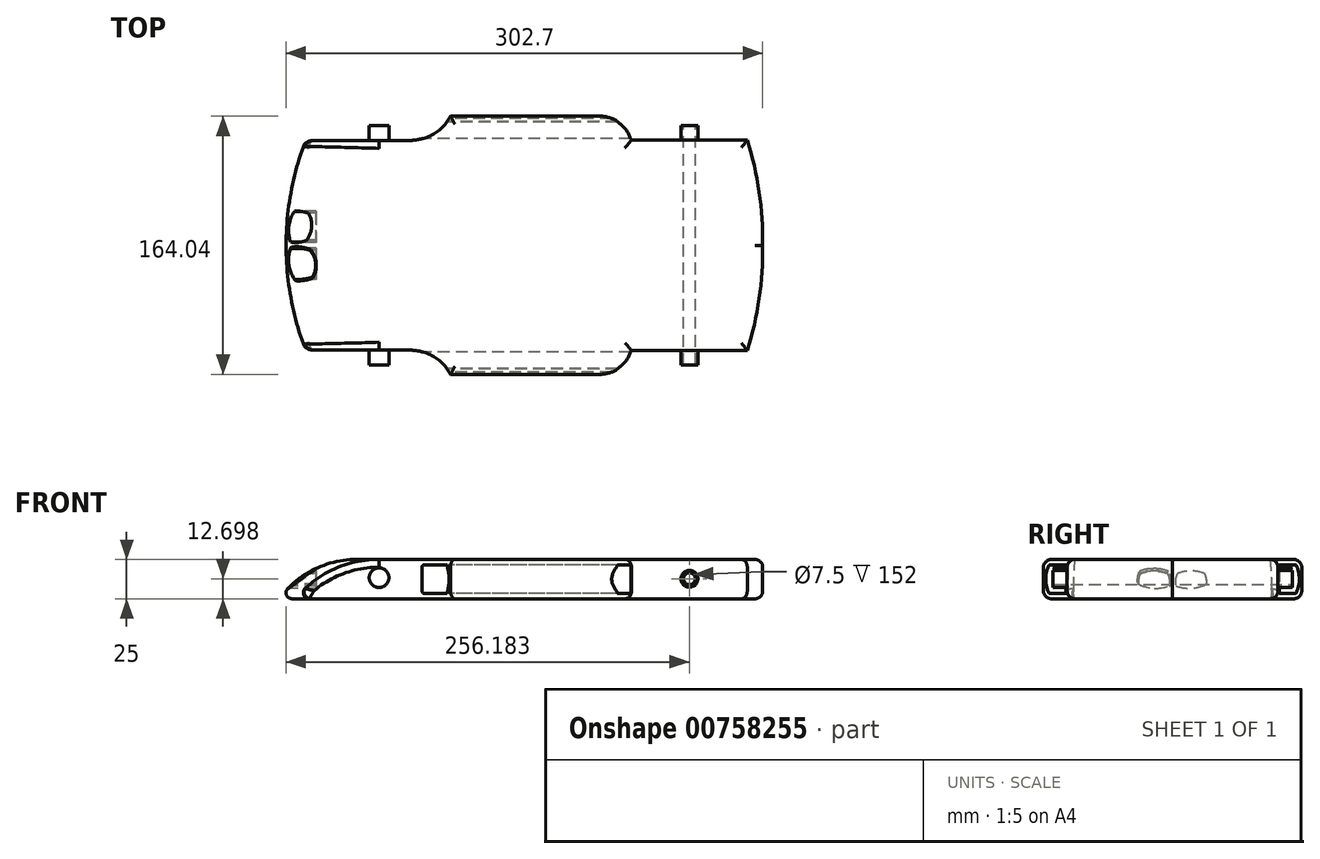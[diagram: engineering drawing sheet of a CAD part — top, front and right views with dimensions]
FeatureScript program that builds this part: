
annotation { "Feature Type Name" : "Feature", "Feature Type Description" : "" }
export const myFeature = defineFeature(function(context is Context, id is Id, definition is map)
    precondition{}
    {
        {
            var Q0;
            Q0=qCreatedBy(makeId("Top.planeOp"),FACE);
            var sketch = newSketch(context, id + "F0", { "sketchPlane" : qUnion([Q0])});
            skArc(sketch, "E0", {"start": v(-145.93, 0) * mm, "mid": v(-142.88, -33.83) * mm, "end": v(-133.85, -66.57) * mm});
            skLineSegment(sketch, "E1", {"start": v(-133.85, -66.57) * mm, "end": v(-63.46, -66.57) * mm});
            skArc(sketch, "E2", {"start": v(-37.18, -82.02) * mm, "mid": v(-48.22, -70.72) * mm, "end": v(-63.46, -66.57) * mm});
            skLineSegment(sketch, "E3", {"start": v(-37.18, -82.02) * mm, "end": v(57.44, -82.02) * mm});
            skArc(sketch, "E4", {"start": v(57.44, -82.02) * mm, "mid": v(70.1, -77.84) * mm, "end": v(77.8, -66.96) * mm});
            skLineSegment(sketch, "E5", {"start": v(77.8, -66.96) * mm, "end": v(151.34, -66.96) * mm});
            skArc(sketch, "E6", {"start": v(151.34, -66.96) * mm, "mid": v(158.9, -33.87) * mm, "end": v(161.11, 0) * mm});
            skArc(sketch, "E7.MirrorCS", {"start": v(-145.93, 0) * mm, "mid": v(-142.88, 33.83) * mm, "end": v(-133.85, 66.57) * mm});
            skLineSegment(sketch, "E8.MirrorCS", {"start": v(-133.85, 66.57) * mm, "end": v(-63.46, 66.57) * mm});
            skArc(sketch, "E9.MirrorCS", {"start": v(-37.18, 82.02) * mm, "mid": v(-48.22, 70.72) * mm, "end": v(-63.46, 66.57) * mm});
            skLineSegment(sketch, "E10.MirrorCS", {"start": v(-37.18, 82.02) * mm, "end": v(57.44, 82.02) * mm});
            skArc(sketch, "E11.MirrorCS", {"start": v(57.44, 82.02) * mm, "mid": v(70.1, 77.84) * mm, "end": v(77.8, 66.96) * mm});
            skLineSegment(sketch, "E12.MirrorCS", {"start": v(77.8, 66.96) * mm, "end": v(151.34, 66.96) * mm});
            skArc(sketch, "E13.MirrorCS", {"start": v(151.34, 66.96) * mm, "mid": v(158.9, 33.87) * mm, "end": v(161.11, 0) * mm});
            skSolve(sketch);
        }
        {
            var Q0;
            Q0 = qSketchRegion(id + "F0", true);
            extrude(context, id + "F1", {"entities" : qUnion([Q0]), "depth" : 25 * mm, "offsetDistance" : 25 * mm});
        }
        {
            var Q0;
            Q0=makeQuery(id+"F1.opExtrude","CAP_EDGE",EDGE,{"disambiguationData":[OSD([sQuery(id+"F0.wireOp",EDGE,"E0")])],"isStart":false});
            fillet(context, id + "F2", {"entities" : qUnion([Q0]), "radius" : 61.08 * mm, "tangentPropagation" : true, "allowEdgeOverflow" : false});
        }
        {
            var Q0;
            {var subQ0=sQuery(id+"F0.wireOp",EDGE,"E0");Q0=makeQuery(id+"F2.opFillet","BLEND_EDGE",EDGE,{"blendedFrom":[makeQuery(id+"F1.opExtrude","CAP_EDGE",EDGE,{"disambiguationData":[OSD([subQ0])],"isStart":false}),makeQuery(id+"F1.opExtrude","CAP_FACE",FACE,{"disambiguationData":[OSD([subQ0,sQuery(id+"F0.wireOp",EDGE,"E1"),sQuery(id+"F0.wireOp",EDGE,"E2"),sQuery(id+"F0.wireOp",EDGE,"E3"),sQuery(id+"F0.wireOp",EDGE,"E4"),sQuery(id+"F0.wireOp",EDGE,"E5"),sQuery(id+"F0.wireOp",EDGE,"E6"),sQuery(id+"F0.wireOp",EDGE,"E7.MirrorCS"),sQuery(id+"F0.wireOp",EDGE,"E8.MirrorCS"),sQuery(id+"F0.wireOp",EDGE,"E9.MirrorCS"),sQuery(id+"F0.wireOp",EDGE,"E10.MirrorCS"),sQuery(id+"F0.wireOp",EDGE,"E11.MirrorCS"),sQuery(id+"F0.wireOp",EDGE,"E12.MirrorCS"),sQuery(id+"F0.wireOp",EDGE,"E13.MirrorCS")])],"isStart":true})],"blendedInto":[makeQuery(id+"F1.opExtrude","CAP_FACE",FACE,{"disambiguationData":[OSD([subQ0,sQuery(id+"F0.wireOp",EDGE,"E1"),sQuery(id+"F0.wireOp",EDGE,"E2"),sQuery(id+"F0.wireOp",EDGE,"E3"),sQuery(id+"F0.wireOp",EDGE,"E4"),sQuery(id+"F0.wireOp",EDGE,"E5"),sQuery(id+"F0.wireOp",EDGE,"E6"),sQuery(id+"F0.wireOp",EDGE,"E7.MirrorCS"),sQuery(id+"F0.wireOp",EDGE,"E8.MirrorCS"),sQuery(id+"F0.wireOp",EDGE,"E9.MirrorCS"),sQuery(id+"F0.wireOp",EDGE,"E10.MirrorCS"),sQuery(id+"F0.wireOp",EDGE,"E11.MirrorCS"),sQuery(id+"F0.wireOp",EDGE,"E12.MirrorCS"),sQuery(id+"F0.wireOp",EDGE,"E13.MirrorCS")])],"isStart":true})]});}
            fillet(context, id + "F3", {"entities" : qUnion([Q0]), "radius" : 3.8 * mm, "tangentPropagation" : true, "allowEdgeOverflow" : false});
        }
        {
            var Q0;
            Q0=makeQuery(id+"F1.opExtrude","CAP_EDGE",EDGE,{"disambiguationData":[OSD([sQuery(id+"F0.wireOp",EDGE,"E10.MirrorCS")])],"isStart":false});
            var Q1;
            Q1=makeQuery(id+"F1.opExtrude","CAP_EDGE",EDGE,{"disambiguationData":[OSD([sQuery(id+"F0.wireOp",EDGE,"E10.MirrorCS")])],"isStart":true});
            var Q2;
            Q2=makeQuery(id+"F1.opExtrude","CAP_EDGE",EDGE,{"disambiguationData":[OSD([sQuery(id+"F0.wireOp",EDGE,"E9.MirrorCS")])],"isStart":false});
            var Q3;
            Q3=makeQuery(id+"F1.opExtrude","CAP_EDGE",EDGE,{"disambiguationData":[OSD([sQuery(id+"F0.wireOp",EDGE,"E3")])],"isStart":false});
            var Q4;
            Q4=makeQuery(id+"F1.opExtrude","CAP_EDGE",EDGE,{"disambiguationData":[OSD([sQuery(id+"F0.wireOp",EDGE,"E3")])],"isStart":true});
            var Q5;
            Q5=makeQuery(id+"F1.opExtrude","CAP_EDGE",EDGE,{"disambiguationData":[OSD([sQuery(id+"F0.wireOp",EDGE,"E2")])],"isStart":true});
            var Q6;
            Q6=makeQuery(id+"F1.opExtrude","CAP_EDGE",EDGE,{"disambiguationData":[OSD([sQuery(id+"F0.wireOp",EDGE,"E5")])],"isStart":true});
            var Q7;
            Q7=makeQuery(id+"F1.opExtrude","CAP_EDGE",EDGE,{"disambiguationData":[OSD([sQuery(id+"F0.wireOp",EDGE,"E5")])],"isStart":false});
            var Q8;
            Q8=makeQuery(id+"F1.opExtrude","CAP_EDGE",EDGE,{"disambiguationData":[OSD([sQuery(id+"F0.wireOp",EDGE,"E12.MirrorCS")])],"isStart":true});
            var Q9;
            Q9=makeQuery(id+"F1.opExtrude","CAP_EDGE",EDGE,{"disambiguationData":[OSD([sQuery(id+"F0.wireOp",EDGE,"E12.MirrorCS")])],"isStart":false});
            var Q10;
            Q10=makeQuery(id+"F1.opExtrude","CAP_EDGE",EDGE,{"disambiguationData":[OSD([sQuery(id+"F0.wireOp",EDGE,"E6")])],"isStart":false});
            var Q11;
            Q11=makeQuery(id+"F1.opExtrude","CAP_EDGE",EDGE,{"disambiguationData":[OSD([sQuery(id+"F0.wireOp",EDGE,"E6")])],"isStart":true});
            fillet(context, id + "F4", {"entities" : qUnion([Q0, Q1, Q2, Q3, Q4, Q5, Q6, Q7, Q8, Q9, Q10, Q11]), "radius" : 5 * mm, "tangentPropagation" : true, "allowEdgeOverflow" : false});
        }
        {
            var Q0;
            Q0=qCreatedBy(makeId("Front.planeOp"),FACE);
            var sketch = newSketch(context, id + "F5", { "sketchPlane" : qUnion([Q0])});
            skCircle(sketch, "E14", {"center": v(114.62, 12.7) * mm, "radius": 5.35 * mm});
            skCircle(sketch, "E15", {"center": v(114.62, 12.7) * mm, "radius": 3.75 * mm});
            skSolve(sketch);
        }
        {
            var Q0;
            Q0 = qSketchRegion(id + "F5", true);
            extrude(context, id + "F6", {"entities" : qUnion([Q0]), "operationType" : NewBodyOperationType.ADD, "depth" : 76 * mm, "offsetDistance" : 25 * mm, "hasSecondDirection" : true, "secondDirectionOppositeDirection" : true, "secondDirectionDepth" : 76 * mm});
        }
        {
            var Q0;
            Q0=makeQuery(id+"F6.boolean.opBoolean","SPLIT",FACE,{"disambiguationData":[TD([makeQuery(id+"F6.opExtrude","SWEPT_FACE",FACE,{"disambiguationData":[OSD([sQuery(id+"F5.wireOp",EDGE,"E15")])]})])],"derivedFrom":makeQuery(id+"F1.opExtrude","SWEPT_FACE",FACE,{"disambiguationData":[OSD([sQuery(id+"F0.wireOp",EDGE,"E5")])]})});
            extrude(context, id + "F7", {"entities" : qUnion([Q0]), "operationType" : NewBodyOperationType.REMOVE, "endBound" : BoundingType.THROUGH_ALL, "oppositeDirection" : true, "depth" : 25 * mm, "offsetDistance" : 25 * mm});
        }
        {
            var Q0;
            Q0=qCreatedBy(makeId("Right.planeOp"),FACE);
            cPlane(context, id + "F8", {"entities" : qUnion([Q0]), "cplaneType" : CPlaneType.OFFSET, "offset" : 137 * mm, "oppositeDirection" : true, "width" : 150 * mm, "height" : 150 * mm});
        }
        {
            var Q0;
            Q0=qCreatedBy(id+"F8.planeOp",FACE);
            var sketch = newSketch(context, id + "F9", { "sketchPlane" : qUnion([Q0])});
            skPoint(sketch, "E16.start.orphan", {"position": v(0, 8.15) * mm});
            skArc(sketch, "E17", {"start": v(-2.08, 8.15) * mm, "mid": v(-1.81, 12.22) * mm, "end": v(-3.18, 16.06) * mm});
            skArc(sketch, "E18", {"start": v(-3.18, 16.06) * mm, "mid": v(-11.77, 17.65) * mm, "end": v(-20.37, 16.06) * mm});
            skArc(sketch, "E19", {"start": v(-20.37, 16.06) * mm, "mid": v(-21.52, 12.78) * mm, "end": v(-21.59, 9.3) * mm});
            skArc(sketch, "E20", {"start": v(-21.59, 9.3) * mm, "mid": v(-11.96, 6.7) * mm, "end": v(-2.08, 8.15) * mm});
            skArc(sketch, "E21.MirrorCS", {"start": v(3.18, 16.06) * mm, "mid": v(11.77, 17.65) * mm, "end": v(20.37, 16.06) * mm});
            skArc(sketch, "E22.MirrorCS", {"start": v(20.37, 16.06) * mm, "mid": v(21.52, 12.78) * mm, "end": v(21.59, 9.3) * mm});
            skArc(sketch, "E23.MirrorCS", {"start": v(21.59, 9.3) * mm, "mid": v(11.96, 6.7) * mm, "end": v(2.08, 8.15) * mm});
            skArc(sketch, "E24.MirrorCS", {"start": v(2.08, 8.15) * mm, "mid": v(1.81, 12.22) * mm, "end": v(3.18, 16.06) * mm});
            skSolve(sketch);
        }
        {
            var Q0;
            Q0 = qSketchRegion(id + "F9", true);
            extrude(context, id + "F10", {"entities" : qUnion([Q0]), "operationType" : NewBodyOperationType.REMOVE, "depth" : 14.6 * mm, "offsetDistance" : 25 * mm, "hasSecondDirection" : true, "secondDirectionOppositeDirection" : true, "secondDirectionDepth" : 7 * mm});
        }
        {
            var Q0;
            Q0=makeQuery(id+"F10.boolean.opBoolean","INTERSECT",EDGE,{"derivedFrom":[makeQuery(id+"F2.opFillet","BLEND_FACE",FACE,{"disambiguationData":[OSD([sQuery(id+"F0.wireOp",EDGE,"E0")])]}),makeQuery(id+"F10.opExtrude","SWEPT_FACE",FACE,{"disambiguationData":[OSD([sQuery(id+"F9.wireOp",EDGE,"E22.MirrorCS")])]})]});
            var Q1;
            Q1=makeQuery(id+"F10.boolean.opBoolean","INTERSECT",EDGE,{"derivedFrom":[makeQuery(id+"F2.opFillet","BLEND_FACE",FACE,{"disambiguationData":[OSD([sQuery(id+"F0.wireOp",EDGE,"E0")])]}),makeQuery(id+"F10.opExtrude","SWEPT_FACE",FACE,{"disambiguationData":[OSD([sQuery(id+"F9.wireOp",EDGE,"E24.MirrorCS")])]})]});
            var Q2;
            Q2=makeQuery(id+"F10.boolean.opBoolean","INTERSECT",EDGE,{"derivedFrom":[makeQuery(id+"F2.opFillet","BLEND_FACE",FACE,{"disambiguationData":[OSD([sQuery(id+"F0.wireOp",EDGE,"E0")])]}),makeQuery(id+"F10.opExtrude","SWEPT_FACE",FACE,{"disambiguationData":[OSD([sQuery(id+"F9.wireOp",EDGE,"E21.MirrorCS")])]})]});
            var Q3;
            {var subQ0=sQuery(id+"F0.wireOp",EDGE,"E0");Q3=makeQuery(id+"F3.opFillet","BLEND_EDGE",EDGE,{"blendedFrom":[makeQuery(id+"F2.opFillet","BLEND_EDGE",EDGE,{"blendedFrom":[makeQuery(id+"F1.opExtrude","CAP_EDGE",EDGE,{"disambiguationData":[OSD([subQ0])],"isStart":false}),makeQuery(id+"F1.opExtrude","CAP_FACE",FACE,{"disambiguationData":[OSD([subQ0,sQuery(id+"F0.wireOp",EDGE,"E1"),sQuery(id+"F0.wireOp",EDGE,"E2"),sQuery(id+"F0.wireOp",EDGE,"E3"),sQuery(id+"F0.wireOp",EDGE,"E4"),sQuery(id+"F0.wireOp",EDGE,"E5"),sQuery(id+"F0.wireOp",EDGE,"E6"),sQuery(id+"F0.wireOp",EDGE,"E7.MirrorCS"),sQuery(id+"F0.wireOp",EDGE,"E8.MirrorCS"),sQuery(id+"F0.wireOp",EDGE,"E9.MirrorCS"),sQuery(id+"F0.wireOp",EDGE,"E10.MirrorCS"),sQuery(id+"F0.wireOp",EDGE,"E11.MirrorCS"),sQuery(id+"F0.wireOp",EDGE,"E12.MirrorCS"),sQuery(id+"F0.wireOp",EDGE,"E13.MirrorCS")])],"isStart":true})],"blendedInto":[makeQuery(id+"F1.opExtrude","CAP_FACE",FACE,{"disambiguationData":[OSD([subQ0,sQuery(id+"F0.wireOp",EDGE,"E1"),sQuery(id+"F0.wireOp",EDGE,"E2"),sQuery(id+"F0.wireOp",EDGE,"E3"),sQuery(id+"F0.wireOp",EDGE,"E4"),sQuery(id+"F0.wireOp",EDGE,"E5"),sQuery(id+"F0.wireOp",EDGE,"E6"),sQuery(id+"F0.wireOp",EDGE,"E7.MirrorCS"),sQuery(id+"F0.wireOp",EDGE,"E8.MirrorCS"),sQuery(id+"F0.wireOp",EDGE,"E9.MirrorCS"),sQuery(id+"F0.wireOp",EDGE,"E10.MirrorCS"),sQuery(id+"F0.wireOp",EDGE,"E11.MirrorCS"),sQuery(id+"F0.wireOp",EDGE,"E12.MirrorCS"),sQuery(id+"F0.wireOp",EDGE,"E13.MirrorCS")])],"isStart":true})]}),makeQuery(id+"F2.opFillet","BLEND_FACE",FACE,{"disambiguationData":[OSD([subQ0])]})],"blendedInto":[makeQuery(id+"F2.opFillet","BLEND_FACE",FACE,{"disambiguationData":[OSD([subQ0])]})]});}
            var Q4;
            Q4=makeQuery(id+"F10.boolean.opBoolean","INTERSECT",EDGE,{"derivedFrom":[makeQuery(id+"F2.opFillet","BLEND_FACE",FACE,{"disambiguationData":[OSD([sQuery(id+"F0.wireOp",EDGE,"E0")])]}),makeQuery(id+"F10.opExtrude","SWEPT_FACE",FACE,{"disambiguationData":[OSD([sQuery(id+"F9.wireOp",EDGE,"E18")])]})]});
            var Q5;
            Q5=makeQuery(id+"F10.boolean.opBoolean","INTERSECT",EDGE,{"derivedFrom":[makeQuery(id+"F2.opFillet","BLEND_FACE",FACE,{"disambiguationData":[OSD([sQuery(id+"F0.wireOp",EDGE,"E0")])]}),makeQuery(id+"F10.opExtrude","SWEPT_FACE",FACE,{"disambiguationData":[OSD([sQuery(id+"F9.wireOp",EDGE,"E19")])]})]});
            var Q6;
            Q6=makeQuery(id+"F10.boolean.opBoolean","INTERSECT",EDGE,{"derivedFrom":[makeQuery(id+"F2.opFillet","BLEND_FACE",FACE,{"disambiguationData":[OSD([sQuery(id+"F0.wireOp",EDGE,"E0")])]}),makeQuery(id+"F10.opExtrude","SWEPT_FACE",FACE,{"disambiguationData":[OSD([sQuery(id+"F9.wireOp",EDGE,"E17")])]})]});
            fillet(context, id + "F11", {"entities" : qUnion([Q0, Q1, Q2, Q3, Q4, Q5, Q6]), "radius" : 0.81 * mm, "tangentPropagation" : true, "allowEdgeOverflow" : false});
        }
        {
            var Q0;
            Q0=qCreatedBy(makeId("Right.planeOp"),FACE);
            var sketch = newSketch(context, id + "F12", { "sketchPlane" : qUnion([Q0])});
            skArc(sketch, "E25", {"start": v(-78.45, 21.45) * mm, "mid": v(-80.55, 12.4) * mm, "end": v(-78.38, 3.36) * mm});
            skLineSegment(sketch, "E26", {"start": v(-78.38, 3.36) * mm, "end": v(-67.7, 3.36) * mm});
            skLineSegment(sketch, "E27", {"start": v(-67.7, 3.36) * mm, "end": v(-67.7, 21.45) * mm});
            skLineSegment(sketch, "E28", {"start": v(-67.7, 21.45) * mm, "end": v(-78.45, 21.45) * mm});
            skLineSegment(sketch, "E29.MirrorCS", {"start": v(67.7, 21.45) * mm, "end": v(78.45, 21.45) * mm});
            skArc(sketch, "E30.MirrorCS", {"start": v(78.45, 21.45) * mm, "mid": v(80.55, 12.4) * mm, "end": v(78.38, 3.36) * mm});
            skLineSegment(sketch, "E31.MirrorCS", {"start": v(78.38, 3.36) * mm, "end": v(67.7, 3.36) * mm});
            skLineSegment(sketch, "E32.MirrorCS", {"start": v(67.7, 3.36) * mm, "end": v(67.7, 21.45) * mm});
            skSolve(sketch);
        }
        {
            var Q0;
            Q0 = qSketchRegion(id + "F12", true);
            extrude(context, id + "F13", {"entities" : qUnion([Q0]), "operationType" : NewBodyOperationType.REMOVE, "depth" : 81.5 * mm, "offsetDistance" : 25 * mm, "hasSecondDirection" : true, "secondDirectionOppositeDirection" : true, "secondDirectionDepth" : 64.2 * mm});
        }
        {
            var Q0;
            Q0=qCreatedBy(makeId("Front.planeOp"),FACE);
            var sketch = newSketch(context, id + "F14", { "sketchPlane" : qUnion([Q0])});
            skCircle(sketch, "E33", {"center": v(-82.49, 13.38) * mm, "radius": 6.25 * mm});
            skSolve(sketch);
        }
        {
            var Q0;
            Q0 = qSketchRegion(id + "F14", true);
            extrude(context, id + "F15", {"entities" : qUnion([Q0]), "operationType" : NewBodyOperationType.ADD, "depth" : 76 * mm, "offsetDistance" : 25 * mm, "hasSecondDirection" : true, "secondDirectionOppositeDirection" : true, "secondDirectionDepth" : 76 * mm});
        }
    });
